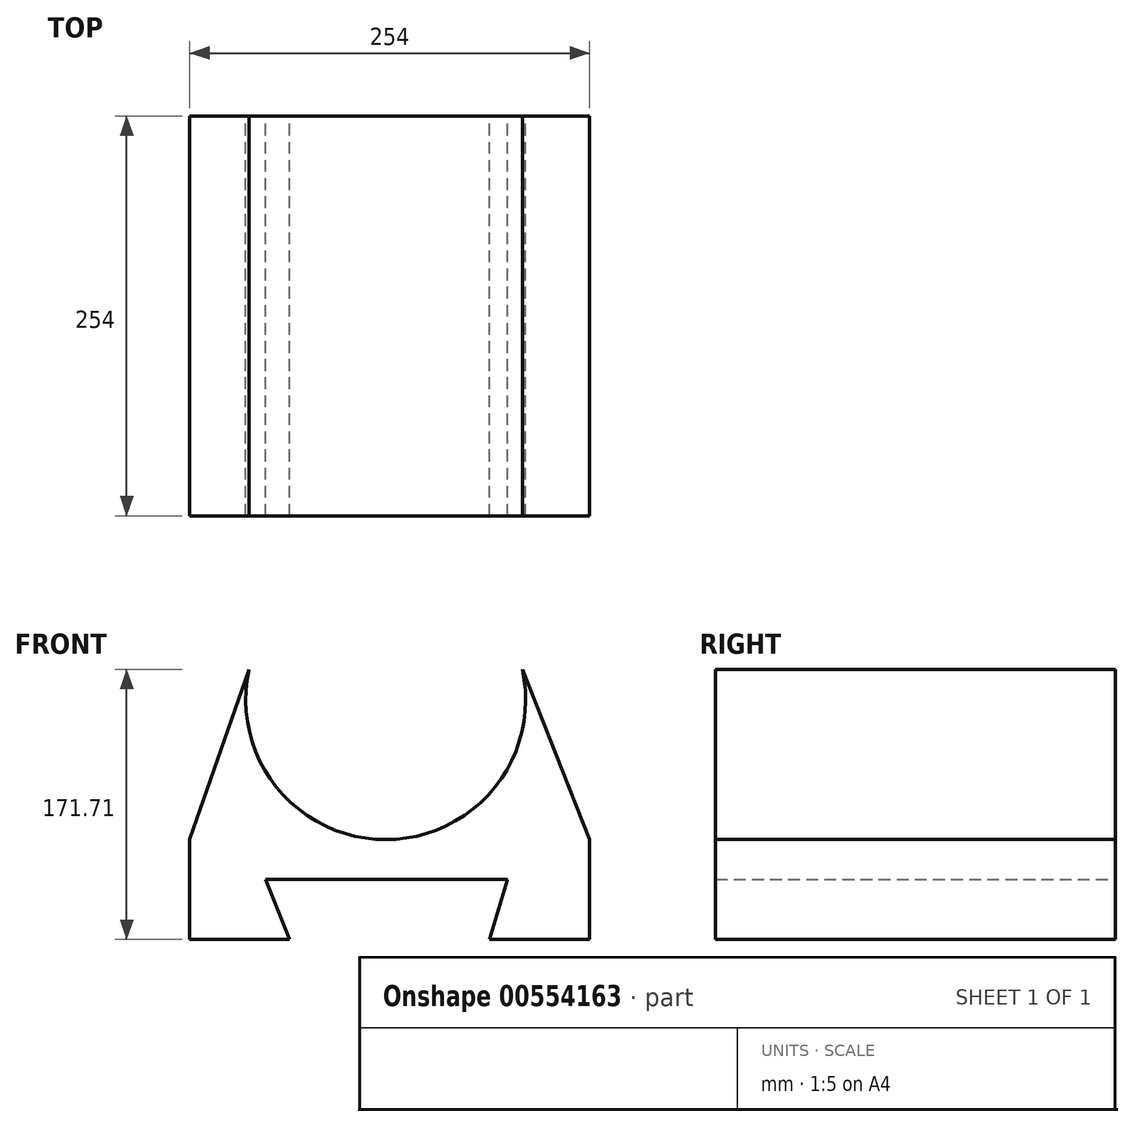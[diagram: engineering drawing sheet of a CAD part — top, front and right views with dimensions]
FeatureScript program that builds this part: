
annotation { "Feature Type Name" : "Feature", "Feature Type Description" : "" }
export const myFeature = defineFeature(function(context is Context, id is Id, definition is map)
    precondition{}
    {
        {
            var Q0;
            Q0=qCreatedBy(makeId("Front.planeOp"),FACE);
            var sketch = newSketch(context, id + "F0", { "sketchPlane" : qUnion([Q0])});
            skLineSegment(sketch, "E0", {"start": v(0, 0) * mm, "end": v(254, 0) * mm});
            skLineSegment(sketch, "E1", {"start": v(0, 0) * mm, "end": v(0, -63.5) * mm});
            skLineSegment(sketch, "E2", {"start": v(254, 0) * mm, "end": v(254, -63.5) * mm});
            skLineSegment(sketch, "E3", {"start": v(254, -63.5) * mm, "end": v(190.5, -63.5) * mm});
            skLineSegment(sketch, "E4", {"start": v(0, -63.5) * mm, "end": v(63.5, -63.5) * mm});
            skCircle(sketch, "E5", {"center": v(124.41, 88.9) * mm, "radius": 88.9 * mm});
            skCircle(sketch, "E6", {"center": v(124.41, 88.9) * mm, "radius": 50.8 * mm});
            skLineSegment(sketch, "E7", {"start": v(63.5, -63.5) * mm, "end": v(48.04, -25.4) * mm});
            skLineSegment(sketch, "E8", {"start": v(48.04, -25.4) * mm, "end": v(201.77, -25.4) * mm});
            skLineSegment(sketch, "E9", {"start": v(201.77, -25.4) * mm, "end": v(190.5, -63.5) * mm});
            skLineSegment(sketch, "E10", {"start": v(0, 0) * mm, "end": v(37.63, 108.2) * mm});
            skLineSegment(sketch, "E11", {"start": v(211.19, 108.2) * mm, "end": v(254, 0) * mm});
            skSolve(sketch);
        }
        {
            var Q0;
            {var subQ1=sQuery(id+"F0.wireOp",EDGE,"E1");Q0=makeQuery(id+"F0.imprint","IMPRINT",FACE,{"disambiguationData":[TD([[makeQuery(id+"F0.imprint","IMPRINT",EDGE,{"derivedFrom":subQ1}),1.0]])]});}
            var Q1;
            {var subQ0=sQuery(id+"F0.wireOp",EDGE,"E10");Q1=makeQuery(id+"F0.imprint","IMPRINT",FACE,{"disambiguationData":[TD([[makeQuery(id+"F0.imprint","IMPRINT",EDGE,{"derivedFrom":subQ0}),-1.0]])]});}
            var Q2;
            {var subQ0=sQuery(id+"F0.wireOp",EDGE,"E11");Q2=makeQuery(id+"F0.imprint","IMPRINT",FACE,{"disambiguationData":[TD([[makeQuery(id+"F0.imprint","IMPRINT",EDGE,{"derivedFrom":subQ0}),-1.0]])]});}
            extrude(context, id + "F1", {"entities" : qUnion([Q0, Q1, Q2]), "depth" : 254 * mm, "offsetDistance" : 25.4 * mm});
        }
    });
